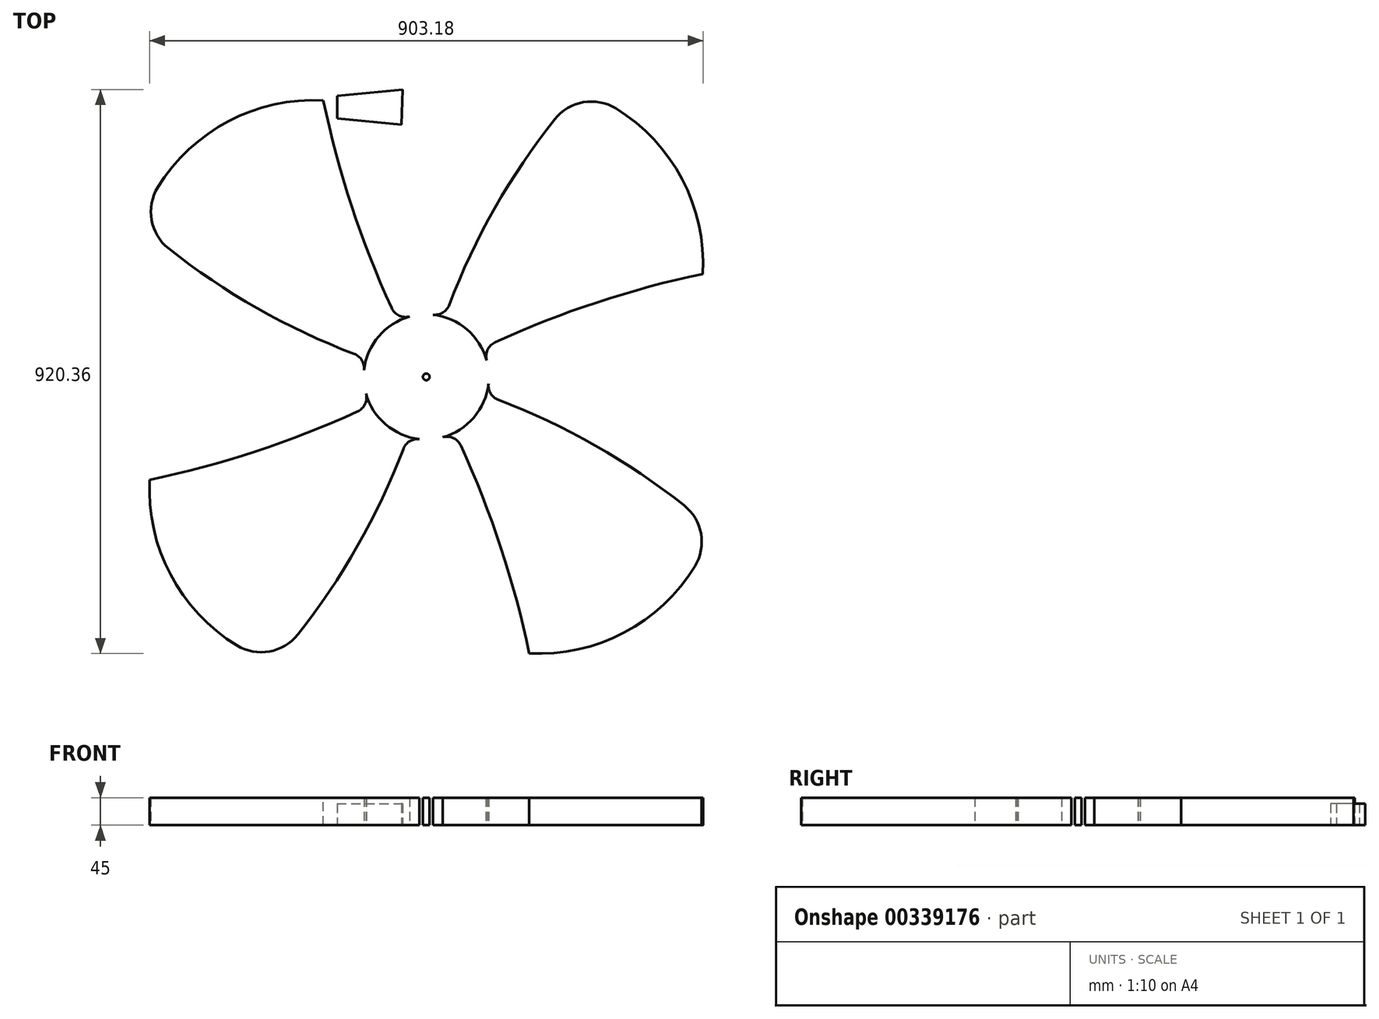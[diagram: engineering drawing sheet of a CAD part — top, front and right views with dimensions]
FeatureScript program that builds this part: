
annotation { "Feature Type Name" : "Feature", "Feature Type Description" : "" }
export const myFeature = defineFeature(function(context is Context, id is Id, definition is map)
    precondition{}
    {
        {
            var Q0;
            Q0=qCreatedBy(makeId("Top.planeOp"),FACE);
            var sketch = newSketch(context, id + "F0", { "sketchPlane" : qUnion([Q0])});
            skCircle(sketch, "E0", {"center": v(0, -106.12) * mm, "radius": 102.05 * mm});
            skArc(sketch, "E1", {"start": v(-168.06, 345.05) * mm, "mid": v(-322.67, 311.22) * mm, "end": v(-438.15, 203) * mm});
            skArc(sketch, "E2", {"start": v(-420.5, 103.52) * mm, "mid": v(-275.7, 5.82) * mm, "end": v(-117.67, -68.57) * mm});
            skArc(sketch, "E3", {"start": v(-168.06, 345.05) * mm, "mid": v(-121.72, 172.6) * mm, "end": v(-56.67, 6.29) * mm});
            skArc(sketch, "E4", {"start": v(-438.15, 203) * mm, "mid": v(-448.17, 149.91) * mm, "end": v(-420.5, 103.52) * mm});
            skArc(sketch, "E5", {"start": v(-451.17, -274.17) * mm, "mid": v(-417.34, -428.79) * mm, "end": v(-309.1, -544.27) * mm});
            skArc(sketch, "E6", {"start": v(-209.64, -526.61) * mm, "mid": v(-111.94, -381.82) * mm, "end": v(-37.54, -223.8) * mm});
            skArc(sketch, "E7", {"start": v(-451.17, -274.17) * mm, "mid": v(-278.7, -227.84) * mm, "end": v(-112.4, -162.79) * mm});
            skArc(sketch, "E8", {"start": v(-309.1, -544.27) * mm, "mid": v(-256.03, -554.3) * mm, "end": v(-209.64, -526.61) * mm});
            skArc(sketch, "E9", {"start": v(168.06, -557.28) * mm, "mid": v(322.67, -523.46) * mm, "end": v(438.15, -415.22) * mm});
            skArc(sketch, "E10", {"start": v(420.5, -315.76) * mm, "mid": v(275.7, -218.05) * mm, "end": v(117.67, -143.66) * mm});
            skArc(sketch, "E11", {"start": v(168.06, -557.28) * mm, "mid": v(121.72, -384.82) * mm, "end": v(56.67, -218.52) * mm});
            skArc(sketch, "E12", {"start": v(438.15, -415.22) * mm, "mid": v(448.17, -362.14) * mm, "end": v(420.5, -315.76) * mm});
            skArc(sketch, "E13", {"start": v(451.17, 61.94) * mm, "mid": v(417.34, 216.56) * mm, "end": v(309.1, 332.03) * mm});
            skArc(sketch, "E14", {"start": v(209.64, 314.38) * mm, "mid": v(111.94, 169.6) * mm, "end": v(37.54, 11.56) * mm});
            skArc(sketch, "E15", {"start": v(451.17, 61.94) * mm, "mid": v(278.7, 15.6) * mm, "end": v(112.4, -49.45) * mm});
            skArc(sketch, "E16", {"start": v(309.1, 332.03) * mm, "mid": v(256.03, 342.06) * mm, "end": v(209.64, 314.38) * mm});
            skArc(sketch, "E17", {"start": v(-101.45, -95.07) * mm, "mid": v(-105.04, -79.05) * mm, "end": v(-117.67, -68.57) * mm});
            skArc(sketch, "E18", {"start": v(-56.67, 6.29) * mm, "mid": v(-44.34, -6.17) * mm, "end": v(-26.87, -7.67) * mm});
            skArc(sketch, "E19", {"start": v(-112.4, -162.79) * mm, "mid": v(-99.95, -150.45) * mm, "end": v(-98.44, -132.99) * mm});
            skArc(sketch, "E20", {"start": v(-11.05, -207.56) * mm, "mid": v(-27.07, -211.15) * mm, "end": v(-37.54, -223.8) * mm});
            skArc(sketch, "E21", {"start": v(56.67, -218.52) * mm, "mid": v(44.34, -206.06) * mm, "end": v(26.87, -204.56) * mm});
            skArc(sketch, "E22", {"start": v(101.45, -117.17) * mm, "mid": v(105.04, -133.18) * mm, "end": v(117.67, -143.66) * mm});
            skArc(sketch, "E23", {"start": v(112.4, -49.45) * mm, "mid": v(99.95, -61.78) * mm, "end": v(98.44, -79.24) * mm});
            skArc(sketch, "E24", {"start": v(11.05, -4.67) * mm, "mid": v(27.07, -1.08) * mm, "end": v(37.54, 11.56) * mm});
            skArc(sketch, "E25", {"start": v(405.87, -188.96) * mm, "mid": v(455.8, -90.64) * mm, "end": v(483.94, 15.98) * mm});
            skArc(sketch, "E26", {"start": v(546.67, -204.95) * mm, "mid": v(542.56, -86.75) * mm, "end": v(483.94, 15.98) * mm});
            skEllipticalArc(sketch, "E27", {});
            skEllipticalArc(sketch, "E28", {});
            skArc(sketch, "E29", {"start": v(546.67, -204.95) * mm, "mid": v(532.07, -181.34) * mm, "end": v(514.7, -159.68) * mm});
            skArc(sketch, "E30", {"start": v(461.42, -159.68) * mm, "mid": v(433.29, -173.64) * mm, "end": v(405.87, -188.96) * mm});
            skArc(sketch, "E31", {"start": v(-483.94, 15.98) * mm, "mid": v(-455.8, -90.64) * mm, "end": v(-405.87, -188.96) * mm});
            skArc(sketch, "E32", {"start": v(-483.94, 15.98) * mm, "mid": v(-542.56, -86.75) * mm, "end": v(-546.67, -204.95) * mm});
            skArc(sketch, "E33", {"start": v(-514.7, -159.68) * mm, "mid": v(-532.07, -181.34) * mm, "end": v(-546.67, -204.95) * mm});
            skArc(sketch, "E34", {"start": v(-405.87, -188.96) * mm, "mid": v(-433.29, -173.64) * mm, "end": v(-461.42, -159.68) * mm});
            skArc(sketch, "E35", {"start": v(0, -615.24) * mm, "mid": v(-27.79, -572.24) * mm, "end": v(-72.9, -548.02) * mm});
            skArc(sketch, "E36", {"start": v(72.9, -548.02) * mm, "mid": v(27.79, -572.24) * mm, "end": v(0, -615.24) * mm});
            skEllipticalArc(sketch, "E37", {});
            skEllipticalArc(sketch, "E38", {});
            skArc(sketch, "E39", {"start": v(-113.73, -407.57) * mm, "mid": v(-72.4, -384.2) * mm, "end": v(-59.08, -338.63) * mm});
            skLineSegment(sketch, "E40", {"start": v(-145.5, 352.75) * mm, "end": v(-38.76, 362.65) * mm});
            skLineSegment(sketch, "E41", {"start": v(-145.5, 352.75) * mm, "end": v(-145.5, 315.58) * mm});
            skLineSegment(sketch, "E42", {"start": v(-145.5, 315.58) * mm, "end": v(-40.41, 305.84) * mm});
            skLineSegment(sketch, "E43", {"start": v(144.8, 352.75) * mm, "end": v(38.77, 362.63) * mm});
            skLineSegment(sketch, "E44", {"start": v(144.8, 315.58) * mm, "end": v(40.41, 305.86) * mm});
            skCircle(sketch, "E45", {"center": v(0, -106.12) * mm, "radius": 5.44 * mm});
            skEllipticalArc(sketch, "E46", {});
            skEllipticalArc(sketch, "E47", {});
            skEllipticalArc(sketch, "E48", {});
            skEllipticalArc(sketch, "E49", {});
            skLineSegment(sketch, "E50", {"start": v(-38.1, 385.6) * mm, "end": v(-49.36, -3.06) * mm});
            skLineSegment(sketch, "E51", {"start": v(38.1, 385.6) * mm, "end": v(48.16, 38.46) * mm});
            skCircle(sketch, "E52", {"center": v(0, 497.26) * mm, "radius": 68.04 * mm});
            skLineSegment(sketch, "E53", {"start": v(144.8, 352.75) * mm, "end": v(144.8, 315.58) * mm});
            skArc(sketch, "E54", {"start": v(59.08, -338.63) * mm, "mid": v(72.4, -384.2) * mm, "end": v(113.73, -407.57) * mm});
            skArc(sketch, "E55", {"start": v(38.1, 385.6) * mm, "mid": v(0, 615.24) * mm, "end": v(-38.1, 385.6) * mm});
            skLineSegment(sketch, "E56", {"start": v(55.54, -216.33) * mm, "end": v(59.08, -338.63) * mm});
            skLineSegment(sketch, "E57", {"start": v(-57.15, -272.04) * mm, "end": v(-59.08, -338.63) * mm});
            const initialGuessF0  = {"E27": [0, -0.15968050359999983, -18.166049, 0, 0.46141764460000007, 0.25577825400000004, 0, 0.43309], "E28": [0, -0.15968050359999983, -20.263785, 0, 0.514700139, 0.39229769140000004, 0, 0.531867], "E37": [0, -0.15968050359999983, -20.263785, 0, 0.514700139, 0.39229769140000004, 1.712903, 1.892029], "E38": [0, -0.15968050359999983, -18.166049, 0, 0.46141764460000007, 0.25577825400000004, 1.819833, 1.852627], "E46": [0, -0.15968050359999983, -18.166049, 0, 0.46141764460000007, 0.25577825400000004, 1.29439, 1.32176], "E47": [0, -0.15968050359999983, -20.263785, 0, 0.514700139, 0.39229769140000004, 1.162721, 1.42869], "E48": [0, -0.15968050359999983, -20.263785, 0, 0.514700139, 0.39229769140000004, 2.62094, 3.141593], "E49": [0, -0.15968050359999983, -18.166049, 0, 0.46141764460000007, 0.25577825400000004, 2.587742, 3.141593]};
            skSetInitialGuess(sketch, initialGuessF0);
            skSolve(sketch);
        }
        {
            var Q0;
            {var subQ6=sQuery(id+"F0.wireOp",EDGE,"E20");Q0=makeQuery(id+"F0.imprint","IMPRINT",FACE,{"disambiguationData":[TD([[makeQuery(id+"F0.imprint","IMPRINT",EDGE,{"derivedFrom":subQ6}),1.0]])]});}
            var Q1;
            {var subQ0=sQuery(id+"F0.wireOp",EDGE,"E27");Q1=makeQuery(id+"F0.imprint","IMPRINT",FACE,{"disambiguationData":[TD([[makeQuery(id+"F0.imprint","IMPRINT",EDGE,{"derivedFrom":subQ0}),-1.0]])]});}
            var Q2;
            Q2=makeQuery(id+"F0.imprint","IMPRINT",FACE,{"disambiguationData":[TD([[makeQuery(id+"F0.imprint","IMPRINT",EDGE,{"derivedFrom":sQuery(id+"F0.wireOp",EDGE,"E25")}),-1.0]])]});
            var Q3;
            {var subQ3=sQuery(id+"F0.wireOp",EDGE,"E24");Q3=makeQuery(id+"F0.imprint","IMPRINT",FACE,{"disambiguationData":[TD([[makeQuery(id+"F0.imprint","IMPRINT",EDGE,{"derivedFrom":subQ3}),1.0]])]});}
            var Q4;
            {var subQ0=sQuery(id+"F0.wireOp",EDGE,"E43");Q4=makeQuery(id+"F0.imprint","IMPRINT",FACE,{"disambiguationData":[TD([[makeQuery(id+"F0.imprint","IMPRINT",EDGE,{"derivedFrom":subQ0}),1.0]])]});}
            var Q5;
            {var subQ0=sQuery(id+"F0.wireOp",EDGE,"E40");Q5=makeQuery(id+"F0.imprint","IMPRINT",FACE,{"disambiguationData":[TD([[makeQuery(id+"F0.imprint","IMPRINT",EDGE,{"derivedFrom":subQ0}),-1.0]])]});}
            extrude(context, id + "F1", {"entities" : qUnion([Q0, Q1, Q2, Q3, Q4, Q5]), "depth" : 35 * mm});
        }
        {
            var Q0;
            Q0=makeQuery(id+"F0.imprint","IMPRINT",FACE,{"disambiguationData":[TD([[makeQuery(id+"F0.imprint","IMPRINT",EDGE,{"derivedFrom":sQuery(id+"F0.wireOp",EDGE,"E1")}),1.0]])]});
            var Q1;
            {var subQ0=sQuery(id+"F0.wireOp",EDGE,"E8");Q1=makeQuery(id+"F0.imprint","IMPRINT",FACE,{"disambiguationData":[TD([[makeQuery(id+"F0.imprint","IMPRINT",EDGE,{"derivedFrom":subQ0}),1.0]])]});}
            var Q2;
            {var subQ8=sQuery(id+"F0.wireOp",EDGE,"E9");Q2=makeQuery(id+"F0.imprint","IMPRINT",FACE,{"disambiguationData":[TD([[makeQuery(id+"F0.imprint","IMPRINT",EDGE,{"derivedFrom":subQ8}),1.0]])]});}
            var Q3;
            Q3=makeQuery(id+"F0.imprint","IMPRINT",FACE,{"disambiguationData":[TD([[makeQuery(id+"F0.imprint","IMPRINT",EDGE,{"derivedFrom":sQuery(id+"F0.wireOp",EDGE,"E13")}),1.0]])]});
            var Q4;
            Q4=makeQuery(id+"F0.imprint","IMPRINT",FACE,{"disambiguationData":[TD([[makeQuery(id+"F0.imprint","IMPRINT",EDGE,{"derivedFrom":sQuery(id+"F0.wireOp",EDGE,"E45")}),1.0]])]});
            extrude(context, id + "F2", {"entities" : qUnion([Q0, Q1, Q2, Q3, Q4]), "depth" : 45 * mm});
        }
    });
